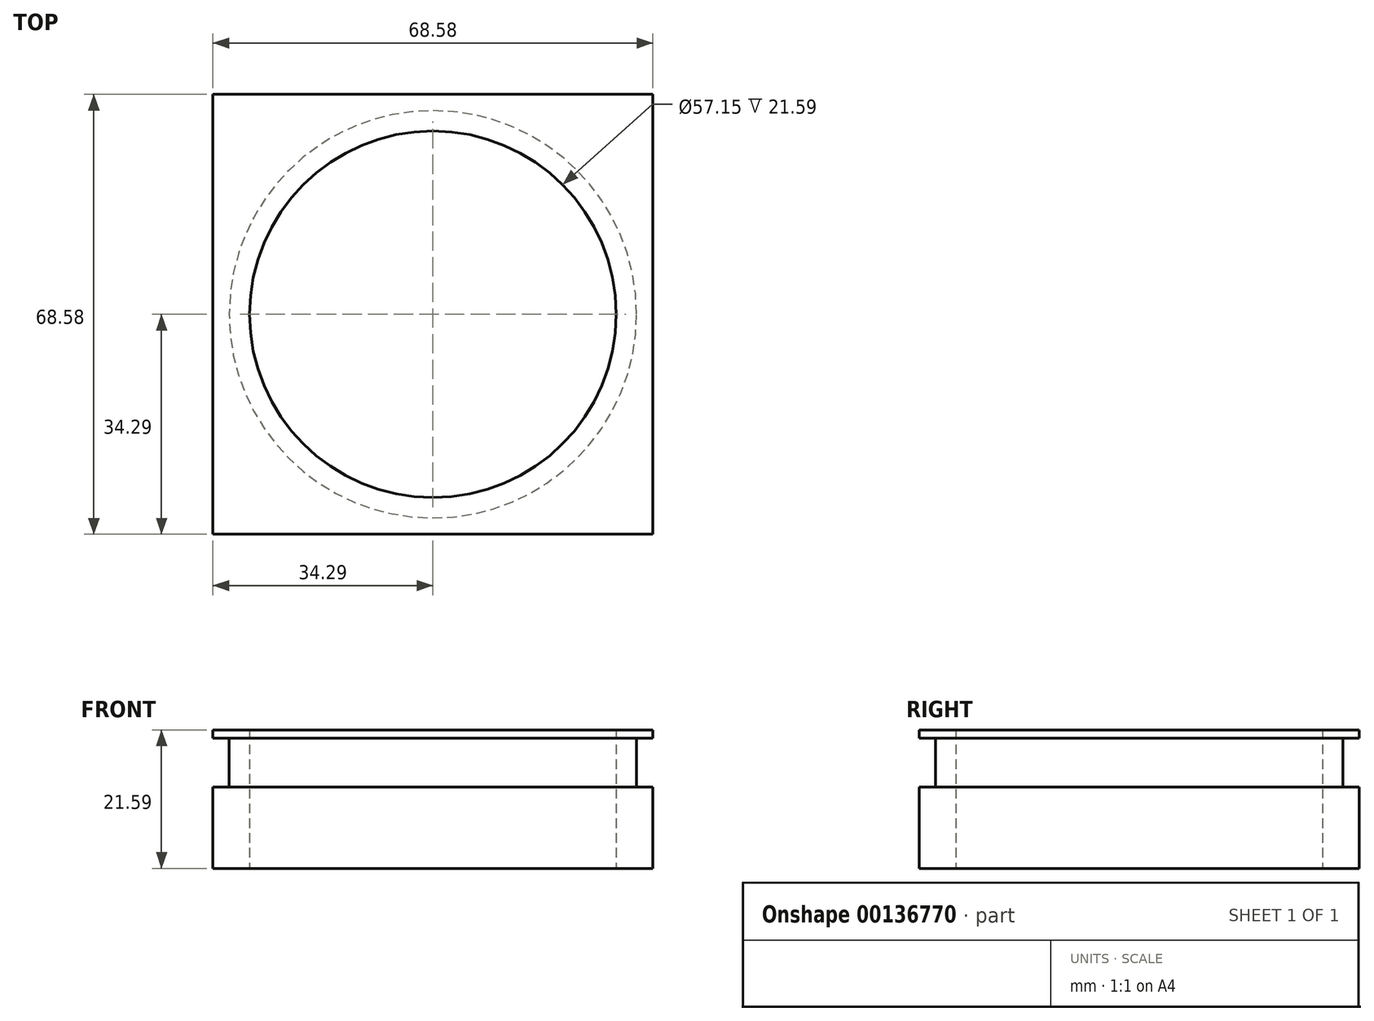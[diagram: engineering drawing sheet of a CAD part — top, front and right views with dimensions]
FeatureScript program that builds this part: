
annotation { "Feature Type Name" : "Feature", "Feature Type Description" : "" }
export const myFeature = defineFeature(function(context is Context, id is Id, definition is map)
    precondition{}
    {
        {
            var Q0;
            Q0=qCreatedBy(makeId("Top.planeOp"),FACE);
            var sketch = newSketch(context, id + "F0", { "sketchPlane" : qUnion([Q0])});
            skLineSegment(sketch, "E0", {"start": v(0, 0) * mm, "end": v(0, 34.3) * mm});
            skLineSegment(sketch, "E1", {"start": v(0, 0) * mm, "end": v(0, -34.3) * mm});
            skLineSegment(sketch, "E2", {"start": v(0, 0) * mm, "end": v(34.3, 0) * mm});
            skLineSegment(sketch, "E3", {"start": v(0, 0) * mm, "end": v(-34.3, 0) * mm});
            skLineSegment(sketch, "E4", {"start": v(-34.3, 0) * mm, "end": v(-34.3, 34.3) * mm});
            skLineSegment(sketch, "E5", {"start": v(-34.3, 34.3) * mm, "end": v(34.3, 34.3) * mm});
            skLineSegment(sketch, "E6", {"start": v(34.3, 34.3) * mm, "end": v(34.3, -34.3) * mm});
            skLineSegment(sketch, "E7", {"start": v(34.3, -34.3) * mm, "end": v(-34.3, -34.3) * mm});
            skLineSegment(sketch, "E8", {"start": v(-34.3, -34.3) * mm, "end": v(-34.3, 0) * mm});
            skCircle(sketch, "E9", {"center": v(0, 0) * mm, "radius": 28.58 * mm});
            skSolve(sketch);
        }
        {
            var Q0;
            Q0 = qSketchRegion(id + "F0", true);
            extrude(context, id + "F1", {"entities" : qUnion([Q0]), "depth" : 12.7 * mm});
        }
        {
            var Q0;
            Q0=makeQuery(id+"F1.opExtrude","CAP_FACE",FACE,{"disambiguationData":[OSD([sQuery(id+"F0.wireOp",EDGE,"E4"),sQuery(id+"F0.wireOp",EDGE,"E5"),sQuery(id+"F0.wireOp",EDGE,"E6"),sQuery(id+"F0.wireOp",EDGE,"E7"),sQuery(id+"F0.wireOp",EDGE,"E8"),sQuery(id+"F0.wireOp",EDGE,"E9")])],"isStart":false});
            var sketch = newSketch(context, id + "F2", { "sketchPlane" : qUnion([Q0])});
            skCircle(sketch, "E10", {"center": v(0, 0) * mm, "radius": 31.75 * mm});
            skCircle(sketch, "E11", {"center": v(0, 0) * mm, "radius": 28.58 * mm});
            skSolve(sketch);
        }
        {
            var Q0;
            Q0 = qSketchRegion(id + "F2", true);
            extrude(context, id + "F3", {"entities" : qUnion([Q0]), "operationType" : NewBodyOperationType.ADD, "depth" : 6.35 * mm});
        }
        {
            var Q0;
            Q0=makeQuery(id+"F3.opExtrude","CAP_FACE",FACE,{"disambiguationData":[OSD([sQuery(id+"F2.wireOp",EDGE,"E10"),sQuery(id+"F2.wireOp",EDGE,"E11")])],"isStart":false});
            cPlane(context, id + "F4", {"entities" : qUnion([Q0]), "cplaneType" : CPlaneType.OFFSET, "offset" : 2.54 * mm, "oppositeDirection" : true, "width" : 152.4 * mm, "height" : 152.4 * mm});
        }
        {
            var Q0;
            Q0=makeQuery(id+"F1.opExtrude","SWEPT_BODY",BODY,{"disambiguationData":[OSD([sQuery(id+"F0.wireOp",EDGE,"E4"),sQuery(id+"F0.wireOp",EDGE,"E5"),sQuery(id+"F0.wireOp",EDGE,"E6"),sQuery(id+"F0.wireOp",EDGE,"E7"),sQuery(id+"F0.wireOp",EDGE,"E8"),sQuery(id+"F0.wireOp",EDGE,"E9")])]});
            var Q1;
            Q1=qCreatedBy(id+"F4.planeOp",FACE);
            mirror(context, id + "F5", {"operationType" : NewBodyOperationType.ADD, "entities" : qUnion([Q0]), "mirrorPlane" : qUnion([Q1])});
        }
        {
            var Q0;
            Q0=makeQuery(id+"F5.opPattern","COPY",FACE,{"derivedFrom":makeQuery(id+"F1.opExtrude","CAP_FACE",FACE,{"disambiguationData":[OSD([sQuery(id+"F0.wireOp",EDGE,"E4"),sQuery(id+"F0.wireOp",EDGE,"E5"),sQuery(id+"F0.wireOp",EDGE,"E6"),sQuery(id+"F0.wireOp",EDGE,"E7"),sQuery(id+"F0.wireOp",EDGE,"E8"),sQuery(id+"F0.wireOp",EDGE,"E9")])],"isStart":true}),"instanceName":"1"});
            extrude(context, id + "F6", {"entities" : qUnion([Q0]), "operationType" : NewBodyOperationType.REMOVE, "oppositeDirection" : true, "depth" : 11.43 * mm});
        }
    });
